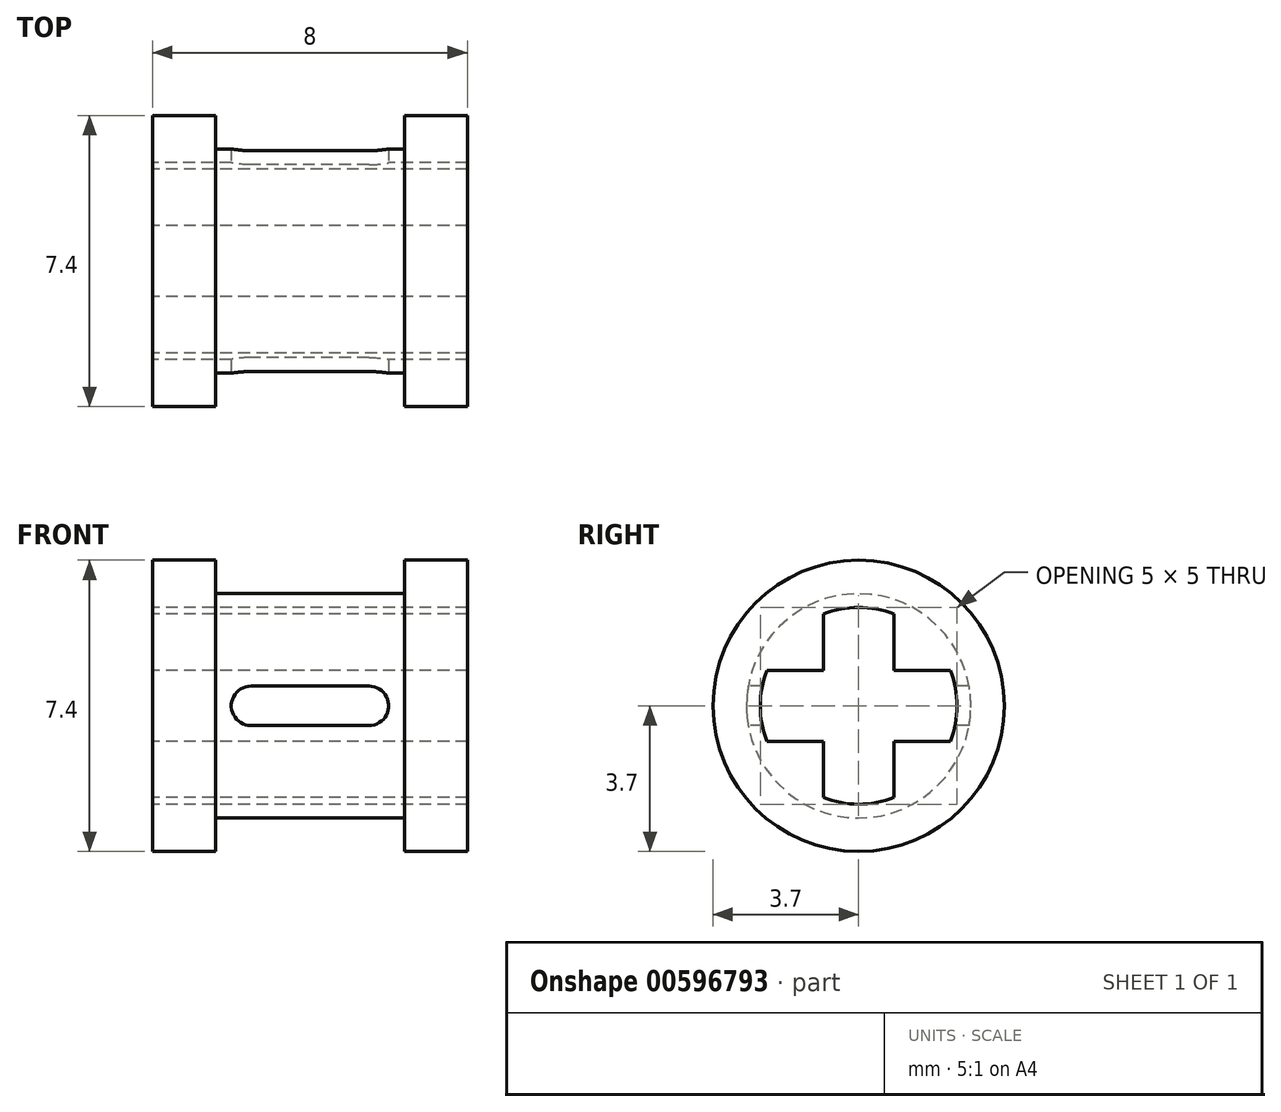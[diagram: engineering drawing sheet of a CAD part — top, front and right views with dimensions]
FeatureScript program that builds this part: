
annotation { "Feature Type Name" : "Feature", "Feature Type Description" : "" }
export const myFeature = defineFeature(function(context is Context, id is Id, definition is map)
    precondition{}
    {
        {
            var Q0;
            Q0=qCreatedBy(makeId("Front.planeOp"),FACE);
            var sketch = newSketch(context, id + "F0", { "sketchPlane" : qUnion([Q0])});
            skLineSegment(sketch, "E0.bottom", {"start": v(4, 3.7) * mm, "end": v(2.4, 3.7) * mm});
            skLineSegment(sketch, "E0.left", {"start": v(4, 3.7) * mm, "end": v(4, 0) * mm});
            skLineSegment(sketch, "E0.right", {"start": v(-4, 3.7) * mm, "end": v(-4, 0) * mm});
            skPoint(sketch, "E0.middle", {"position": v(0, 0) * mm});
            skLineSegment(sketch, "E1.bottom", {"start": v(2.4, 2.85) * mm, "end": v(-2.4, 2.85) * mm});
            skLineSegment(sketch, "E1.left", {"start": v(4, 2.85) * mm, "end": v(4, 0) * mm});
            skLineSegment(sketch, "E1.right", {"start": v(-4, 2.85) * mm, "end": v(-4, 0) * mm});
            skLineSegment(sketch, "E2.bottom", {"start": v(-4, 3.7) * mm, "end": v(-2.4, 3.7) * mm});
            skLineSegment(sketch, "E2.right", {"start": v(-2.4, 3.7) * mm, "end": v(-2.4, 2.85) * mm});
            skLineSegment(sketch, "E3.trimOffspring", {"start": v(2.4, 2.85) * mm, "end": v(2.4, 3.7) * mm});
            skLineSegment(sketch, "E4", {"start": v(6.57, 0) * mm, "end": v(-9.25, 0) * mm, "construction": true});
            skLineSegment(sketch, "E5.trimOffspring", {"start": v(4, 0) * mm, "end": v(4, 3.7) * mm});
            skLineSegment(sketch, "E6", {"start": v(4, 0) * mm, "end": v(-4, 0) * mm});
            skLineSegment(sketch, "E7.trimOffspring", {"start": v(-2.4, 3.7) * mm, "end": v(-4, 3.7) * mm});
            skLineSegment(sketch, "E8.bottom", {"start": v(1.5, 0.5) * mm, "end": v(-1.5, 0.5) * mm});
            skLineSegment(sketch, "E8.top", {"start": v(1.5, -0.5) * mm, "end": v(-1.5, -0.5) * mm});
            skLineSegment(sketch, "E8.left", {"start": v(2, 0) * mm, "end": v(2, 0) * mm});
            skLineSegment(sketch, "E8.right", {"start": v(-2, 0) * mm, "end": v(-2, 0) * mm});
            skPoint(sketch, "E9.visualSharp", {"position": v(-2, -0.5) * mm});
            skArc(sketch, "E9.filletArc", {"start": v(-2, 0) * mm, "mid": v(-1.85, -0.35) * mm, "end": v(-1.5, -0.5) * mm});
            skPoint(sketch, "E10.visualSharp", {"position": v(-2, 0.5) * mm});
            skArc(sketch, "E10.filletArc", {"start": v(-1.5, 0.5) * mm, "mid": v(-1.85, 0.35) * mm, "end": v(-2, 0) * mm});
            skPoint(sketch, "E11.visualSharp", {"position": v(2, 0.5) * mm});
            skArc(sketch, "E11.filletArc", {"start": v(2, 0) * mm, "mid": v(1.85, 0.35) * mm, "end": v(1.5, 0.5) * mm});
            skPoint(sketch, "E12.visualSharp", {"position": v(2, -0.5) * mm});
            skArc(sketch, "E12.filletArc", {"start": v(1.5, -0.5) * mm, "mid": v(1.85, -0.35) * mm, "end": v(2, 0) * mm});
            skSolve(sketch);
        }
        {
            var Q0;
            Q0=makeQuery(id+"F0.imprint","IMPRINT",FACE,{"disambiguationData":[TD([[makeQuery(id+"F0.imprint","IMPRINT",EDGE,{"derivedFrom":sQuery(id+"F0.wireOp",EDGE,"E1.bottom")}),1.0]])]});
            var Q1;
            Q1=sQuery(id+"F0.wireOp",EDGE,"E4");
            revolve(context, id + "F1", {"entities" : qUnion([Q0]), "axis" : qUnion([Q1]), "revolveType" : RevolveType.FULL});
        }
        {
            var Q0;
            Q0=makeQuery(id+"F1.opRevolve","SWEPT_FACE",FACE,{"disambiguationData":[OSD([sQuery(id+"F0.wireOp",EDGE,"E0.right")])]});
            var sketch = newSketch(context, id + "F2", { "sketchPlane" : qUnion([Q0])});
            skCircle(sketch, "E13", {"center": v(0, 0) * mm, "radius": 2.5 * mm});
            skLineSegment(sketch, "E14", {"start": v(0, 0) * mm, "end": v(0.9, 0) * mm, "construction": true});
            skLineSegment(sketch, "E15", {"start": v(0.9, 0) * mm, "end": v(-0.9, 0) * mm, "construction": true});
            skPoint(sketch, "E15.endSnap0", {"position": v(0.45, 0) * mm});
            skLineSegment(sketch, "E16", {"start": v(0, 0) * mm, "end": v(0, -0.9) * mm, "construction": true});
            skLineSegment(sketch, "E17", {"start": v(0, -0.9) * mm, "end": v(0, 0.9) * mm, "construction": true});
            skPoint(sketch, "E17.endSnap0", {"position": v(0, -0.45) * mm});
            skLineSegment(sketch, "E18", {"start": v(-2.33, 0.9) * mm, "end": v(-0.9, 0.9) * mm});
            skLineSegment(sketch, "E19", {"start": v(-0.9, 0.9) * mm, "end": v(-0.9, 2.33) * mm});
            skLineSegment(sketch, "E20", {"start": v(0.9, 2.33) * mm, "end": v(0.9, 0.9) * mm});
            skLineSegment(sketch, "E21", {"start": v(0.9, 0.9) * mm, "end": v(2.33, 0.9) * mm});
            skLineSegment(sketch, "E22", {"start": v(0.9, -2.33) * mm, "end": v(0.9, -0.9) * mm});
            skLineSegment(sketch, "E23", {"start": v(0.9, -0.9) * mm, "end": v(2.33, -0.9) * mm});
            skLineSegment(sketch, "E24", {"start": v(-0.9, -2.33) * mm, "end": v(-0.9, -0.9) * mm});
            skLineSegment(sketch, "E25", {"start": v(-0.9, -0.9) * mm, "end": v(-2.33, -0.9) * mm});
            skSolve(sketch);
        }
        {
            var Q0;
            {var subQ4=sQuery(id+"F2.wireOp",EDGE,"E18");Q0=makeQuery(id+"F2.imprint","IMPRINT",FACE,{"disambiguationData":[TD([[makeQuery(id+"F2.imprint","IMPRINT",EDGE,{"derivedFrom":subQ4}),-1.0]])]});}
            extrude(context, id + "F3", {"entities" : qUnion([Q0]), "operationType" : NewBodyOperationType.REMOVE, "endBound" : BoundingType.THROUGH_ALL, "oppositeDirection" : true, "depth" : 25 * mm, "offsetDistance" : 25 * mm});
        }
        {
            var Q0;
            {var subQ5=sQuery(id+"F0.wireOp",EDGE,"E8.bottom");Q0=makeQuery(id+"F0.imprint","IMPRINT",FACE,{"disambiguationData":[TD([[makeQuery(id+"F0.imprint","IMPRINT",EDGE,{"derivedFrom":subQ5}),1.0]])]});}
            var Q1;
            {var subQ5=sQuery(id+"F0.wireOp",EDGE,"E8.top");Q1=makeQuery(id+"F0.imprint","IMPRINT",FACE,{"disambiguationData":[TD([[makeQuery(id+"F0.imprint","IMPRINT",EDGE,{"derivedFrom":subQ5}),-1.0]])]});}
            extrude(context, id + "F4", {"entities" : qUnion([Q0, Q1]), "operationType" : NewBodyOperationType.REMOVE, "endBound" : BoundingType.SYMMETRIC, "oppositeDirection" : true, "depth" : 10 * mm, "offsetDistance" : 25 * mm});
        }
    });
